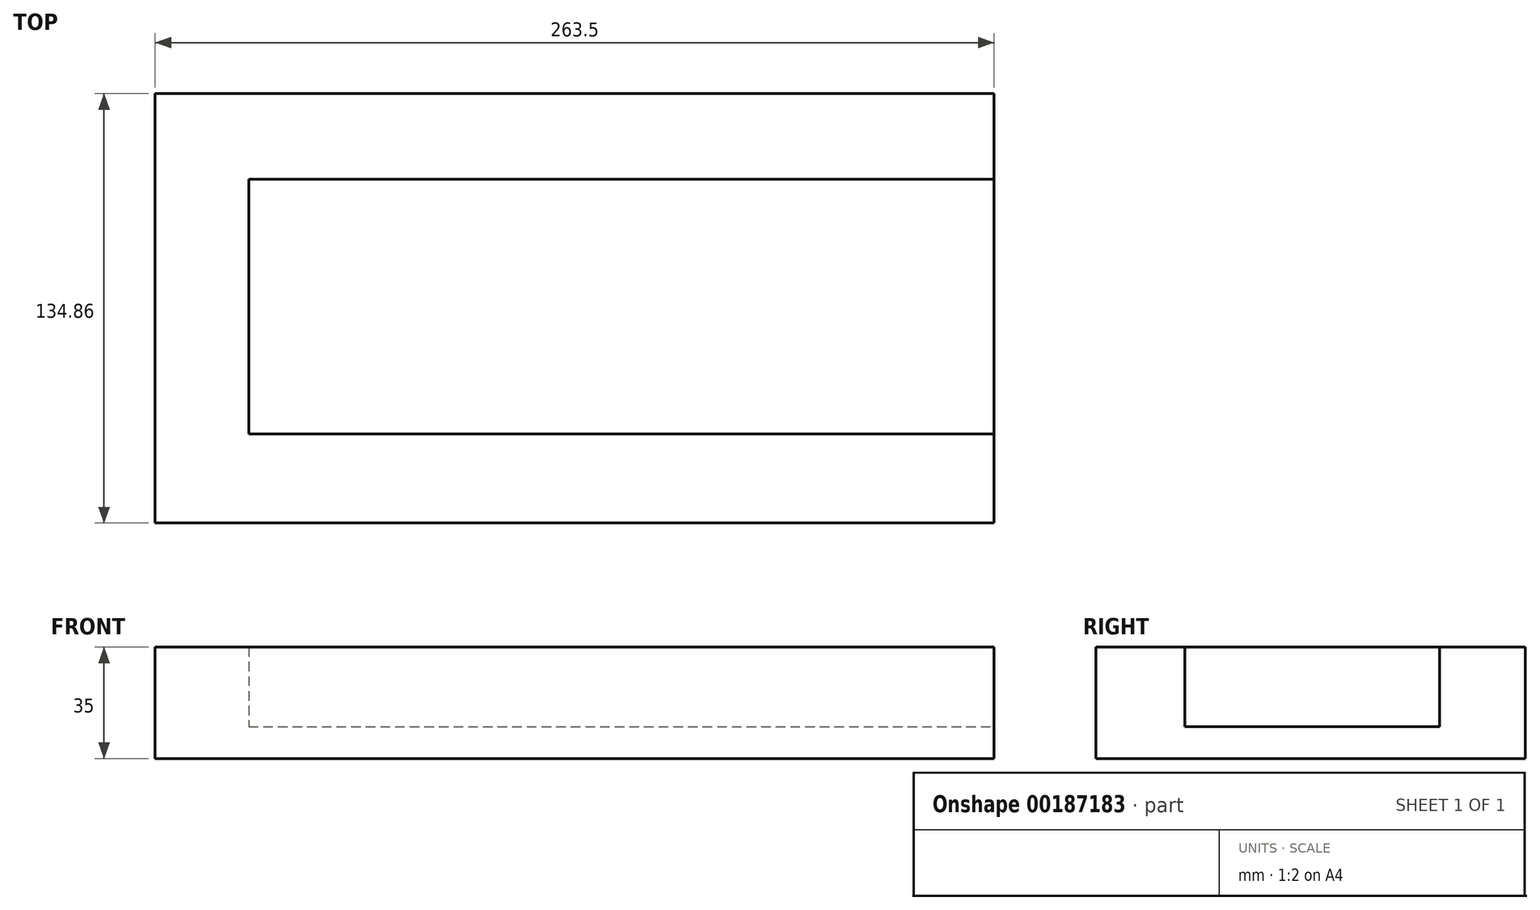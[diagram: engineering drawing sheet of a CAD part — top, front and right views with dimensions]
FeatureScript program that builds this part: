
annotation { "Feature Type Name" : "Feature", "Feature Type Description" : "" }
export const myFeature = defineFeature(function(context is Context, id is Id, definition is map)
    precondition{}
    {
        {
            var Q0;
            Q0=qCreatedBy(makeId("Top.planeOp"),FACE);
            var sketch = newSketch(context, id + "F0", { "sketchPlane" : qUnion([Q0])});
            skLineSegment(sketch, "E0.bottom", {"start": v(-131.75, -67.43) * mm, "end": v(131.75, -67.43) * mm});
            skLineSegment(sketch, "E0.top", {"start": v(-131.75, 67.43) * mm, "end": v(131.75, 67.43) * mm});
            skLineSegment(sketch, "E0.left", {"start": v(-131.75, -67.43) * mm, "end": v(-131.75, 67.43) * mm});
            skLineSegment(sketch, "E0.right", {"start": v(131.75, -67.43) * mm, "end": v(131.75, 67.43) * mm});
            skPoint(sketch, "E0.middle", {"position": v(0, 0) * mm});
            skSolve(sketch);
        }
        {
            var Q0;
            Q0 = qSketchRegion(id + "F0", true);
            extrude(context, id + "F1", {"entities" : qUnion([Q0]), "depth" : 10 * mm});
        }
        {
            var Q0;
            Q0=makeQuery(id+"F1.opExtrude","CAP_FACE",FACE,{"disambiguationData":[OSD([sQuery(id+"F0.wireOp",EDGE,"E0.bottom"),sQuery(id+"F0.wireOp",EDGE,"E0.top"),sQuery(id+"F0.wireOp",EDGE,"E0.left"),sQuery(id+"F0.wireOp",EDGE,"E0.right")])],"isStart":false});
            var sketch = newSketch(context, id + "F2", { "sketchPlane" : qUnion([Q0])});
            skLineSegment(sketch, "E1.bottom", {"start": v(-131.75, 67.43) * mm, "end": v(131.75, 67.43) * mm});
            skLineSegment(sketch, "E1.top", {"start": v(-131.75, -67.43) * mm, "end": v(131.75, -67.43) * mm});
            skLineSegment(sketch, "E1.left", {"start": v(-131.75, 67.43) * mm, "end": v(-131.75, -67.43) * mm});
            skLineSegment(sketch, "E1.right", {"start": v(131.75, 67.43) * mm, "end": v(131.75, 40.57) * mm});
            skLineSegment(sketch, "E2", {"start": v(-102.36, -39.43) * mm, "end": v(131.75, -39.43) * mm});
            skLineSegment(sketch, "E3", {"start": v(-102.36, -39.43) * mm, "end": v(-102.36, 40.57) * mm});
            skLineSegment(sketch, "E4", {"start": v(-102.36, 40.57) * mm, "end": v(131.75, 40.57) * mm});
            skLineSegment(sketch, "E5.trimOffspring", {"start": v(131.75, -39.43) * mm, "end": v(131.75, -67.43) * mm});
            skSolve(sketch);
        }
        {
            var Q0;
            Q0 = qSketchRegion(id + "F2", true);
            extrude(context, id + "F3", {"entities" : qUnion([Q0]), "operationType" : NewBodyOperationType.ADD, "depth" : 25 * mm});
        }
    });
